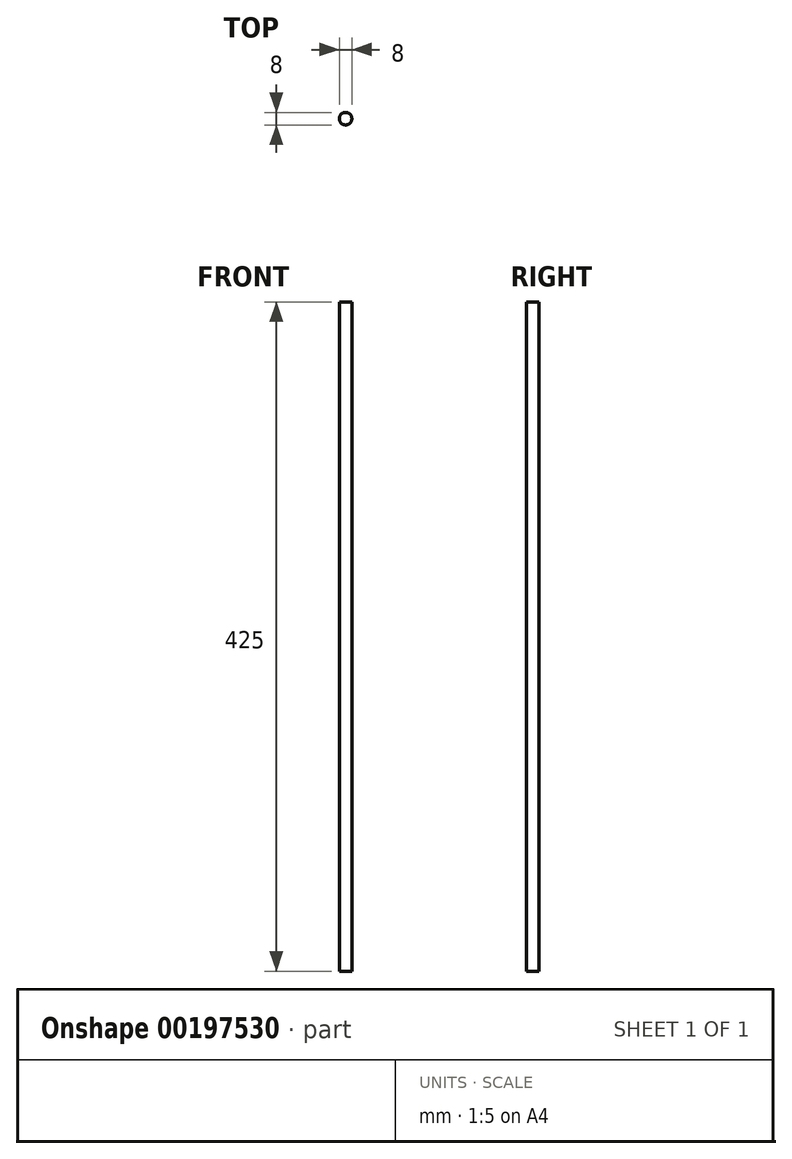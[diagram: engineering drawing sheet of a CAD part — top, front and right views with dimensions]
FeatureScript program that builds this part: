
annotation { "Feature Type Name" : "Feature", "Feature Type Description" : "" }
export const myFeature = defineFeature(function(context is Context, id is Id, definition is map)
    precondition{}
    {
        {
            var Q0;
            Q0=qCreatedBy(makeId("Top.planeOp"),FACE);
            var sketch = newSketch(context, id + "F0", { "sketchPlane" : qUnion([Q0])});
            skCircle(sketch, "E0", {"center": v(0, 0) * mm, "radius": 4 * mm});
            skSolve(sketch);
        }
        {
            var Q0;
            Q0=qSketchRegion(id+"F0",true);
            extrude(context, id + "F1", {"entities" : qUnion([Q0]), "depth" : 425 * mm});
        }
    });
